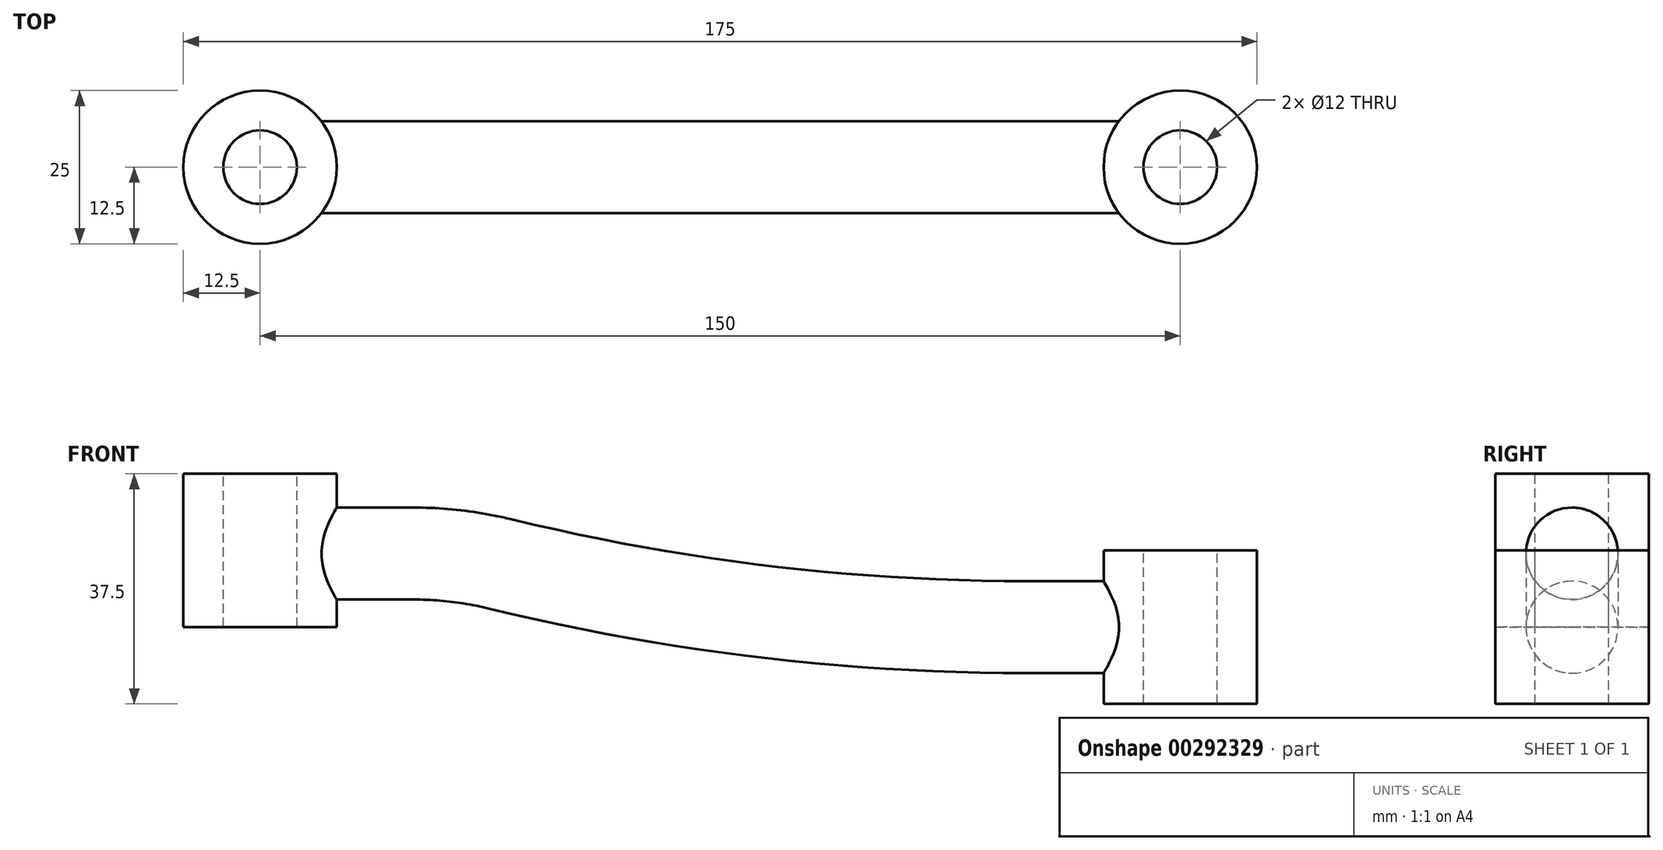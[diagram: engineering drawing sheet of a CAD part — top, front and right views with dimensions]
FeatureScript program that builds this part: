
annotation { "Feature Type Name" : "Feature", "Feature Type Description" : "" }
export const myFeature = defineFeature(function(context is Context, id is Id, definition is map)
    precondition{}
    {
        {
            var Q0;
            Q0=qCreatedBy(makeId("Top.planeOp"),FACE);
            var sketch = newSketch(context, id + "F0", { "sketchPlane" : qUnion([Q0])});
            skCircle(sketch, "E0", {"center": v(0, 0) * mm, "radius": 12.5 * mm});
            skCircle(sketch, "E1", {"center": v(150, 0) * mm, "radius": 12.5 * mm});
            skSolve(sketch);
        }
        {
            var Q0;
            Q0=makeQuery(id+"F0.imprint","IMPRINT",FACE,{"disambiguationData":[TD([[makeQuery(id+"F0.imprint","IMPRINT",EDGE,{"derivedFrom":sQuery(id+"F0.wireOp",EDGE,"E0")}),1.0]])]});
            extrude(context, id + "F1", {"entities" : qUnion([Q0]), "depth" : 25 * mm});
        }
        {
            var Q0;
            Q0=makeQuery(id+"F0.imprint","IMPRINT",FACE,{"disambiguationData":[TD([[makeQuery(id+"F0.imprint","IMPRINT",EDGE,{"derivedFrom":sQuery(id+"F0.wireOp",EDGE,"E1")}),1.0]])]});
            extrude(context, id + "F2", {"entities" : qUnion([Q0]), "endBound" : BoundingType.SYMMETRIC, "depth" : 25 * mm});
        }
        {
            var Q0;
            Q0=qCreatedBy(makeId("Front.planeOp"),FACE);
            var sketch = newSketch(context, id + "F3", { "sketchPlane" : qUnion([Q0])});
            skLineSegment(sketch, "E2", {"start": v(0, 12) * mm, "end": v(25, 12) * mm});
            skArc(sketch, "E3", {"start": v(25, 12) * mm, "mid": v(32.15, 11.57) * mm, "end": v(39.2, 10.3) * mm});
            skArc(sketch, "E4", {"start": v(39.2, 10.3) * mm, "mid": v(81.79, 2.58) * mm, "end": v(125, 0) * mm});
            skLineSegment(sketch, "E5", {"start": v(125, 0) * mm, "end": v(150, 0) * mm});
            skSolve(sketch);
        }
        {
            var Q0;
            Q0=qCreatedBy(makeId("Right.planeOp"),FACE);
            var sketch = newSketch(context, id + "F4", { "sketchPlane" : qUnion([Q0])});
            skCircle(sketch, "E6", {"center": v(0, 12) * mm, "radius": 7.5 * mm});
            skSolve(sketch);
        }
        {
            var Q0;
            Q0 = qSketchRegion(id + "F4", true);
            var Q1;
            Q1 = qConstructionFilter(qBodyType(qCreatedBy(id + "F3" ,EDGE), BodyType.WIRE), ConstructionObject.NO);
            sweep(context, id + "F5", {"operationType" : NewBodyOperationType.ADD, "profiles" : qUnion([Q0]), "path" : qUnion([Q1])});
        }
        {
            var Q0;
            Q0=makeQuery(id+"F1.opExtrude","CAP_FACE",FACE,{"disambiguationData":[OSD([sQuery(id+"F0.wireOp",EDGE,"E0")])],"isStart":false});
            var sketch = newSketch(context, id + "F6", { "sketchPlane" : qUnion([Q0])});
            skCircle(sketch, "E7", {"center": v(0, 0) * mm, "radius": 6 * mm});
            skCircle(sketch, "E8", {"center": v(150, 0) * mm, "radius": 6 * mm});
            skSolve(sketch);
        }
        {
            var Q0;
            Q0=makeQuery(id+"F6.imprint","IMPRINT",FACE,{"disambiguationData":[TD([[makeQuery(id+"F6.imprint","IMPRINT",EDGE,{"derivedFrom":sQuery(id+"F6.wireOp",EDGE,"E7")}),1.0]])]});
            var Q1;
            Q1=makeQuery(id+"F6.imprint","IMPRINT",FACE,{"disambiguationData":[TD([[makeQuery(id+"F6.imprint","IMPRINT",EDGE,{"derivedFrom":sQuery(id+"F6.wireOp",EDGE,"E8")}),1.0]])]});
            extrude(context, id + "F7", {"entities" : qUnion([Q0, Q1]), "operationType" : NewBodyOperationType.REMOVE, "endBound" : BoundingType.THROUGH_ALL, "oppositeDirection" : true, "depth" : 25 * mm});
        }
    });
